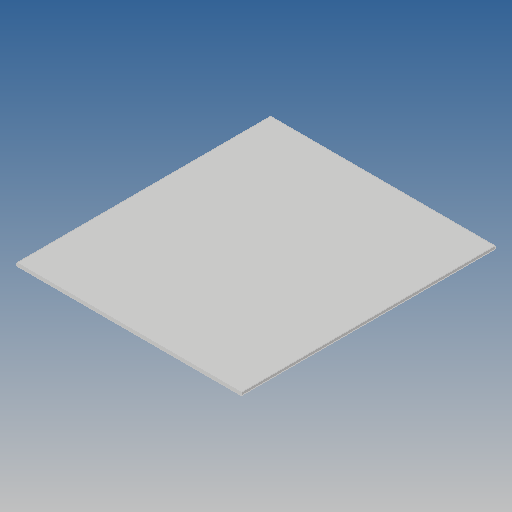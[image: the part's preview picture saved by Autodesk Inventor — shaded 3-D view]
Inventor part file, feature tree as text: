
AUTODESK INVENTOR PART (.ipt)
format: ipt  version: 2018 (Build 220112000, 112)  size: 83,456 bytes
history: native  units: mm
features: other x1, extrude x1, sketch x1
ambient origin geometry x8: Origin, YZ Plane, XZ Plane, XY Plane, X Axis, Y Axis, Z Axis, Center Point
bodies: Solid1 (feature_tree)
feature tree (3):
  other  "<userpath>\OneDrive\Objet3D\3DPrinter\Parameters.xlsx"
  extrude  "Extrusion1"  Depth=520.0mm
  sketch  "Sketch1"  dims[d0=6.0mm d1=0.0mm d2=520.0mm d3=460.0mm]
